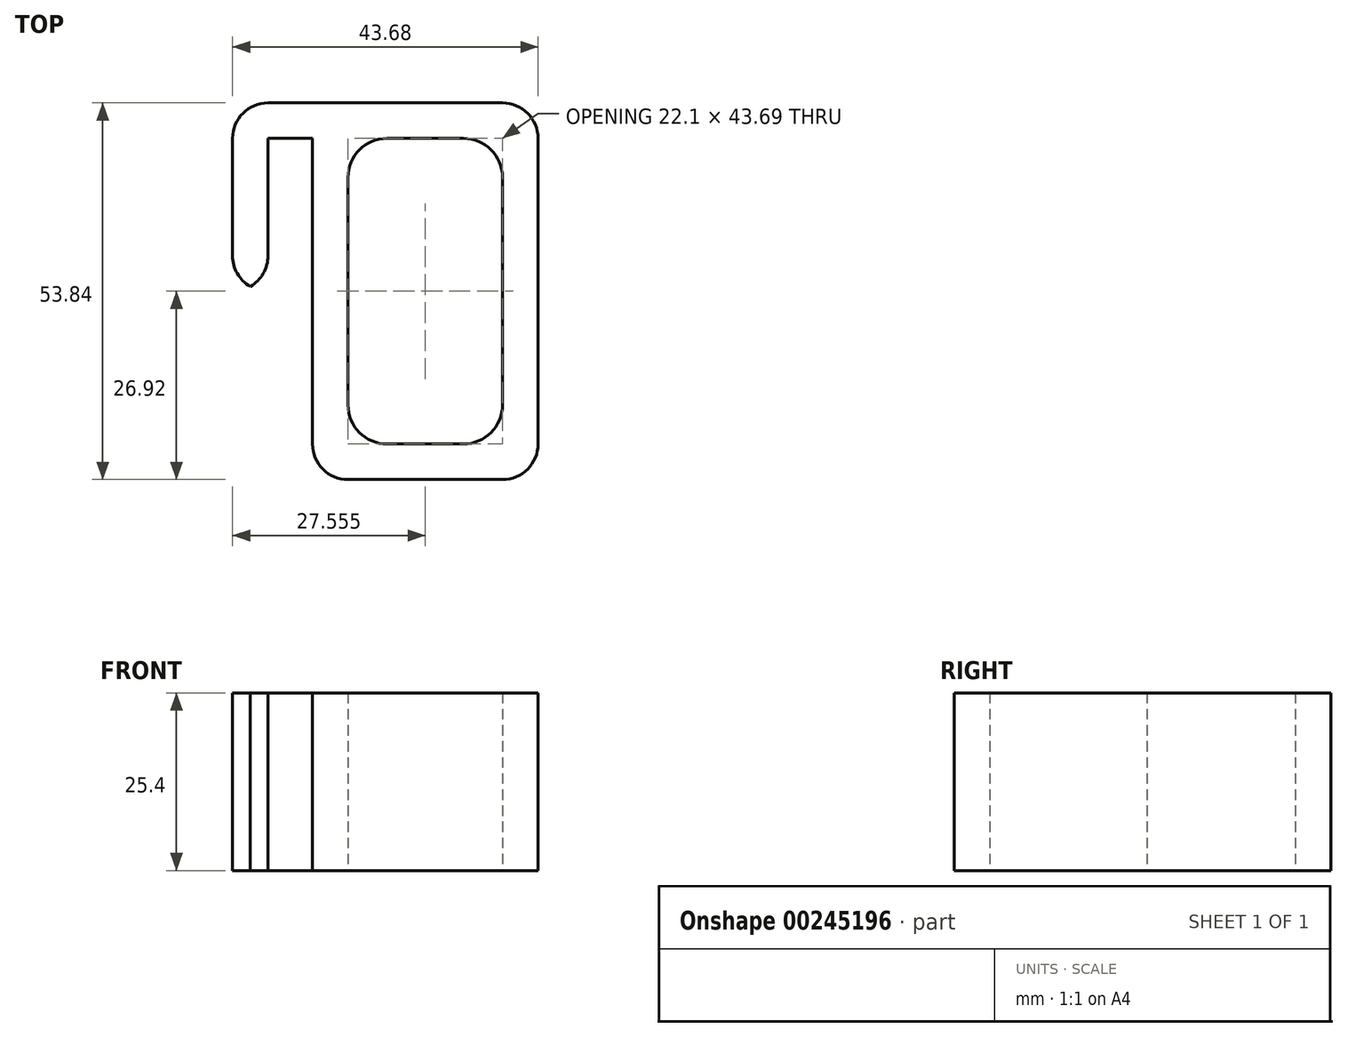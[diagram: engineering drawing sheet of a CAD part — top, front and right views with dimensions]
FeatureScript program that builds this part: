
annotation { "Feature Type Name" : "Feature", "Feature Type Description" : "" }
export const myFeature = defineFeature(function(context is Context, id is Id, definition is map)
    precondition{}
    {
        {
            var Q0;
            Q0=qCreatedBy(makeId("Top.planeOp"),FACE);
            var sketch = newSketch(context, id + "F0", { "sketchPlane" : qUnion([Q0])});
            skLineSegment(sketch, "E0.bottom", {"start": v(21.84, 26.92) * mm, "end": v(-21.84, 26.92) * mm});
            skLineSegment(sketch, "E0.top", {"start": v(21.84, -26.92) * mm, "end": v(-21.84, -26.92) * mm});
            skLineSegment(sketch, "E0.left", {"start": v(21.84, 26.92) * mm, "end": v(21.84, -26.92) * mm});
            skLineSegment(sketch, "E0.right", {"start": v(-21.84, 26.92) * mm, "end": v(-21.84, -26.92) * mm});
            skPoint(sketch, "E0.middle", {"position": v(0, 0) * mm});
            skLineSegment(sketch, "E1.bottom", {"start": v(16.76, 21.84) * mm, "end": v(-5.33, 21.84) * mm});
            skLineSegment(sketch, "E1.top", {"start": v(16.76, -21.84) * mm, "end": v(-5.33, -21.84) * mm});
            skLineSegment(sketch, "E1.left", {"start": v(16.76, 21.84) * mm, "end": v(16.76, -21.84) * mm});
            skLineSegment(sketch, "E1.right", {"start": v(-5.33, 21.84) * mm, "end": v(-5.33, -21.84) * mm});
            skLineSegment(sketch, "E2", {"start": v(-21.84, 0) * mm, "end": v(-16.76, 0) * mm});
            skPoint(sketch, "E2.endSnap0", {"position": v(-21.84, 0) * mm});
            skLineSegment(sketch, "E3", {"start": v(-16.76, 0) * mm, "end": v(-16.76, 21.84) * mm});
            skLineSegment(sketch, "E4", {"start": v(-16.76, 21.84) * mm, "end": v(-10.41, 21.84) * mm});
            skLineSegment(sketch, "E5", {"start": v(-10.41, 21.84) * mm, "end": v(-10.41, -26.92) * mm});
            skSolve(sketch);
        }
        {
            var Q0;
            {var subQ0=sQuery(id+"F0.wireOp",EDGE,"E0.bottom");Q0=makeQuery(id+"F0.imprint","IMPRINT",FACE,{"disambiguationData":[TD([[makeQuery(id+"F0.imprint","IMPRINT",EDGE,{"derivedFrom":subQ0}),1.0]])]});}
            extrude(context, id + "F1", {"entities" : qUnion([Q0]), "depth" : 25.4 * mm});
        }
        {
            var Q0;
            Q0=makeQuery(id+"F1.opExtrude","SWEPT_EDGE",EDGE,{"disambiguationData":[OSD([sQuery(id+"F0.wireOp",EDGE,"E0.bottom"),sQuery(id+"F0.wireOp",EDGE,"E0.right")])]});
            var Q1;
            Q1=makeQuery(id+"F1.opExtrude","SWEPT_EDGE",EDGE,{"disambiguationData":[OSD([sQuery(id+"F0.wireOp",EDGE,"E0.bottom"),sQuery(id+"F0.wireOp",EDGE,"E0.left")])]});
            var Q2;
            Q2=makeQuery(id+"F1.opExtrude","SWEPT_EDGE",EDGE,{"disambiguationData":[OSD([sQuery(id+"F0.wireOp",EDGE,"E0.top"),sQuery(id+"F0.wireOp",EDGE,"E5")])]});
            var Q3;
            Q3=makeQuery(id+"F1.opExtrude","SWEPT_EDGE",EDGE,{"disambiguationData":[OSD([sQuery(id+"F0.wireOp",EDGE,"E0.top"),sQuery(id+"F0.wireOp",EDGE,"E0.left")])]});
            var Q4;
            Q4=makeQuery(id+"F1.opExtrude","SWEPT_EDGE",EDGE,{"disambiguationData":[OSD([sQuery(id+"F0.wireOp",EDGE,"E2"),sQuery(id+"F0.wireOp",EDGE,"E3")])]});
            var Q5;
            Q5=makeQuery(id+"F1.opExtrude","SWEPT_EDGE",EDGE,{"disambiguationData":[OSD([sQuery(id+"F0.wireOp",EDGE,"E0.right"),sQuery(id+"F0.wireOp",EDGE,"E2")])]});
            fillet(context, id + "F2", {"entities" : qUnion([Q0, Q1, Q2, Q3, Q4, Q5]), "radius" : 5.08 * mm, "tangentPropagation" : true, "allowEdgeOverflow" : false});
        }
        {
            var Q0;
            Q0=makeQuery(id+"F1.opExtrude","SWEPT_EDGE",EDGE,{"disambiguationData":[OSD([sQuery(id+"F0.wireOp",EDGE,"E1.top"),sQuery(id+"F0.wireOp",EDGE,"E1.right")])]});
            var Q1;
            Q1=makeQuery(id+"F1.opExtrude","SWEPT_EDGE",EDGE,{"disambiguationData":[OSD([sQuery(id+"F0.wireOp",EDGE,"E1.top"),sQuery(id+"F0.wireOp",EDGE,"E1.left")])]});
            var Q2;
            Q2=makeQuery(id+"F1.opExtrude","SWEPT_EDGE",EDGE,{"disambiguationData":[OSD([sQuery(id+"F0.wireOp",EDGE,"E1.bottom"),sQuery(id+"F0.wireOp",EDGE,"E1.left")])]});
            var Q3;
            Q3=makeQuery(id+"F1.opExtrude","SWEPT_EDGE",EDGE,{"disambiguationData":[OSD([sQuery(id+"F0.wireOp",EDGE,"E1.bottom"),sQuery(id+"F0.wireOp",EDGE,"E1.right")])]});
            fillet(context, id + "F3", {"entities" : qUnion([Q0, Q1, Q2, Q3]), "radius" : 5.6 * mm, "tangentPropagation" : true, "allowEdgeOverflow" : false});
        }
    });
